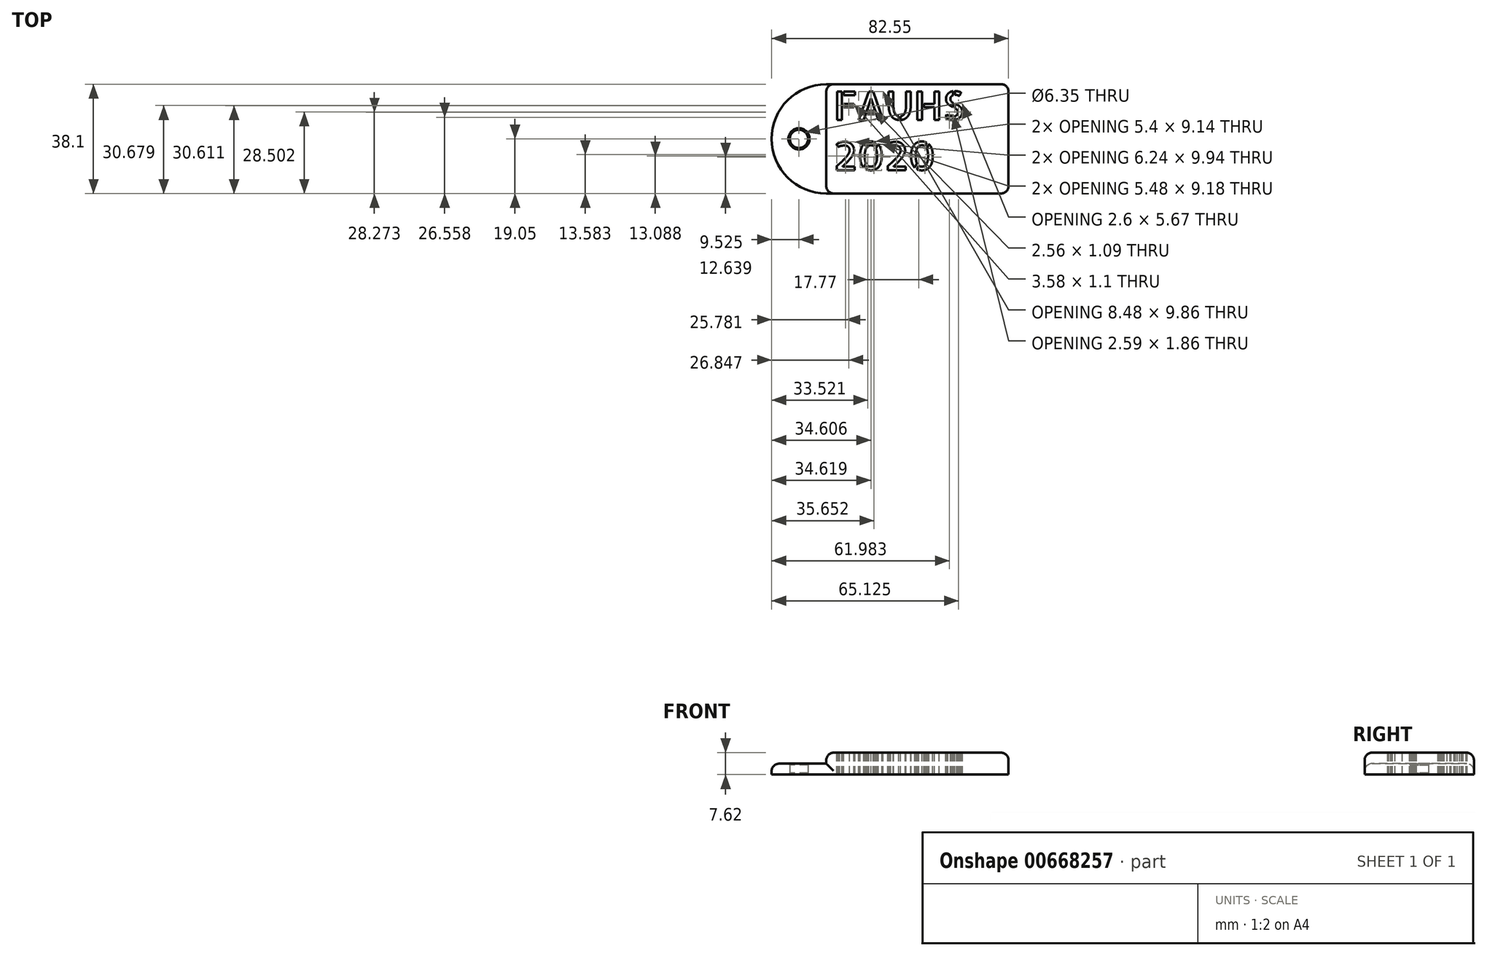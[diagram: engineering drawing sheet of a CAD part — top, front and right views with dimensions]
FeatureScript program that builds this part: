
annotation { "Feature Type Name" : "Feature", "Feature Type Description" : "" }
export const myFeature = defineFeature(function(context is Context, id is Id, definition is map)
    precondition{}
    {
        {
            var Q0;
            Q0=qCreatedBy(makeId("Top.planeOp"),FACE);
            var sketch = newSketch(context, id + "F0", { "sketchPlane" : qUnion([Q0])});
            skLineSegment(sketch, "E0.bottom", {"start": v(31.75, 19.05) * mm, "end": v(-31.75, 19.05) * mm});
            skLineSegment(sketch, "E0.top", {"start": v(31.75, -19.05) * mm, "end": v(-31.75, -19.05) * mm});
            skLineSegment(sketch, "E0.left", {"start": v(31.75, 19.05) * mm, "end": v(31.75, -19.05) * mm});
            skPoint(sketch, "E0.middle", {"position": v(0, 0) * mm});
            skArc(sketch, "E1", {"start": v(-31.75, 19.05) * mm, "mid": v(-50.8, 0) * mm, "end": v(-31.75, -19.05) * mm});
            skPoint(sketch, "E2", {"position": v(-41.28, 0) * mm});
            skCircle(sketch, "E3", {"center": v(-41.28, 0) * mm, "radius": 3.18 * mm});
            skSolve(sketch);
        }
        {
            var Q0;
            Q0 = qSketchRegion(id + "F0", true);
            extrude(context, id + "F1", {"entities" : qUnion([Q0]), "depth" : 3.8 * mm, "offsetDistance" : 25.4 * mm});
        }
        {
            var Q0;
            Q0=makeQuery(id+"F1.opExtrude","CAP_FACE",FACE,{"disambiguationData":[OSD([sQuery(id+"F0.wireOp",EDGE,"E0.bottom"),sQuery(id+"F0.wireOp",EDGE,"E0.top"),sQuery(id+"F0.wireOp",EDGE,"E0.left"),sQuery(id+"F0.wireOp",EDGE,"E1"),sQuery(id+"F0.wireOp",EDGE,"E3")])],"isStart":false});
            var sketch = newSketch(context, id + "F2", { "sketchPlane" : qUnion([Q0])});
            skLineSegment(sketch, "E4.bottom", {"start": v(31.75, -19.05) * mm, "end": v(-31.75, -19.05) * mm});
            skLineSegment(sketch, "E4.top", {"start": v(31.75, 19.05) * mm, "end": v(-31.75, 19.05) * mm});
            skLineSegment(sketch, "E4.left", {"start": v(31.75, -19.05) * mm, "end": v(31.75, 19.05) * mm});
            skLineSegment(sketch, "E4.right", {"start": v(-31.75, -19.05) * mm, "end": v(-31.75, 19.05) * mm});
            skSolve(sketch);
        }
        {
            var Q0;
            Q0 = qSketchRegion(id + "F2", true);
            extrude(context, id + "F3", {"entities" : qUnion([Q0]), "operationType" : NewBodyOperationType.ADD, "depth" : 3.8 * mm, "offsetDistance" : 25.4 * mm});
        }
        {
            var Q0;
            Q0=makeQuery(id+"F1.opExtrude","CAP_EDGE",EDGE,{"disambiguationData":[OSD([sQuery(id+"F0.wireOp",EDGE,"E3")])],"isStart":false});
            var Q1;
            Q1=makeQuery(id+"F1.opExtrude","CAP_EDGE",EDGE,{"disambiguationData":[OSD([sQuery(id+"F0.wireOp",EDGE,"E3")])],"isStart":true});
            chamfer(context, id + "F4", {"entities" : qUnion([Q0, Q1]), "width" : 0.5 * mm, "tangentPropagation" : true});
        }
        {
            var Q0;
            Q0=makeQuery(id+"F1.opExtrude","CAP_EDGE",EDGE,{"disambiguationData":[OSD([sQuery(id+"F0.wireOp",EDGE,"E1")])],"isStart":false});
            var Q1;
            Q1=makeQuery(id+"F3.opExtrude","CAP_EDGE",EDGE,{"disambiguationData":[OSD([sQuery(id+"F2.wireOp",EDGE,"E4.top")])],"isStart":false});
            var Q2;
            Q2=makeQuery(id+"F3.opExtrude","CAP_EDGE",EDGE,{"disambiguationData":[OSD([sQuery(id+"F2.wireOp",EDGE,"E4.right")])],"isStart":false});
            var Q3;
            Q3=makeQuery(id+"F3.opExtrude","CAP_EDGE",EDGE,{"disambiguationData":[OSD([sQuery(id+"F2.wireOp",EDGE,"E4.bottom")])],"isStart":false});
            var Q4;
            Q4=makeQuery(id+"F3.opExtrude","CAP_EDGE",EDGE,{"disambiguationData":[OSD([sQuery(id+"F2.wireOp",EDGE,"E4.left")])],"isStart":false});
            var Q5;
            Q5=makeQuery(id+"F3.opExtrude","SWEPT_EDGE",EDGE,{"disambiguationData":[OSD([sQuery(id+"F0.wireOp",EDGE,"E1"),sQuery(id+"F2.wireOp",EDGE,"E4.bottom"),sQuery(id+"F2.wireOp",EDGE,"E4.right")])]});
            var Q6;
            Q6=makeQuery(id+"F3.boolean.opBoolean","MERGE",EDGE,{"derivedFrom":[makeQuery(id+"F1.opExtrude","SWEPT_EDGE",EDGE,{"disambiguationData":[OSD([sQuery(id+"F0.wireOp",EDGE,"E0.top"),sQuery(id+"F0.wireOp",EDGE,"E0.left")])]}),makeQuery(id+"F3.opExtrude","SWEPT_EDGE",EDGE,{"disambiguationData":[OSD([sQuery(id+"F2.wireOp",EDGE,"E4.bottom"),sQuery(id+"F2.wireOp",EDGE,"E4.left")])]})]});
            var Q7;
            Q7=makeQuery(id+"F3.boolean.opBoolean","MERGE",EDGE,{"derivedFrom":[makeQuery(id+"F1.opExtrude","SWEPT_EDGE",EDGE,{"disambiguationData":[OSD([sQuery(id+"F0.wireOp",EDGE,"E0.bottom"),sQuery(id+"F0.wireOp",EDGE,"E0.left")])]}),makeQuery(id+"F3.opExtrude","SWEPT_EDGE",EDGE,{"disambiguationData":[OSD([sQuery(id+"F2.wireOp",EDGE,"E4.top"),sQuery(id+"F2.wireOp",EDGE,"E4.left")])]})]});
            var Q8;
            Q8=makeQuery(id+"F3.opExtrude","SWEPT_EDGE",EDGE,{"disambiguationData":[OSD([sQuery(id+"F0.wireOp",EDGE,"E1"),sQuery(id+"F2.wireOp",EDGE,"E4.top"),sQuery(id+"F2.wireOp",EDGE,"E4.right")])]});
            fillet(context, id + "F5", {"entities" : qUnion([Q0, Q1, Q2, Q3, Q4, Q5, Q6, Q7, Q8]), "radius" : 2.54 * mm, "tangentPropagation" : true, "allowEdgeOverflow" : false});
        }
        {
            var Q0;
            Q0=makeQuery(id+"F3.opExtrude","CAP_FACE",FACE,{"disambiguationData":[OSD([sQuery(id+"F2.wireOp",EDGE,"E4.bottom"),sQuery(id+"F2.wireOp",EDGE,"E4.top"),sQuery(id+"F2.wireOp",EDGE,"E4.left"),sQuery(id+"F2.wireOp",EDGE,"E4.right")])],"isStart":false});
            var sketch = newSketch(context, id + "F6", { "sketchPlane" : qUnion([Q0])});
            skText(sketch, "E5", { "text": "FAUHS\n2020", "fontName": "AllertaStencil-Regular.ttf"});
            const initialGuessF6  = {"E5": [-0.0292, 0.00663, 1, 0, 0.00988]};
            skSetInitialGuess(sketch, initialGuessF6);
            skSolve(sketch);
        }
        {
            var Q0;
            Q0 = qSketchRegion(id + "F6", true);
            extrude(context, id + "F7", {"entities" : qUnion([Q0]), "operationType" : NewBodyOperationType.REMOVE, "oppositeDirection" : true, "depth" : 25.4 * mm, "offsetDistance" : 25.4 * mm});
        }
    });
